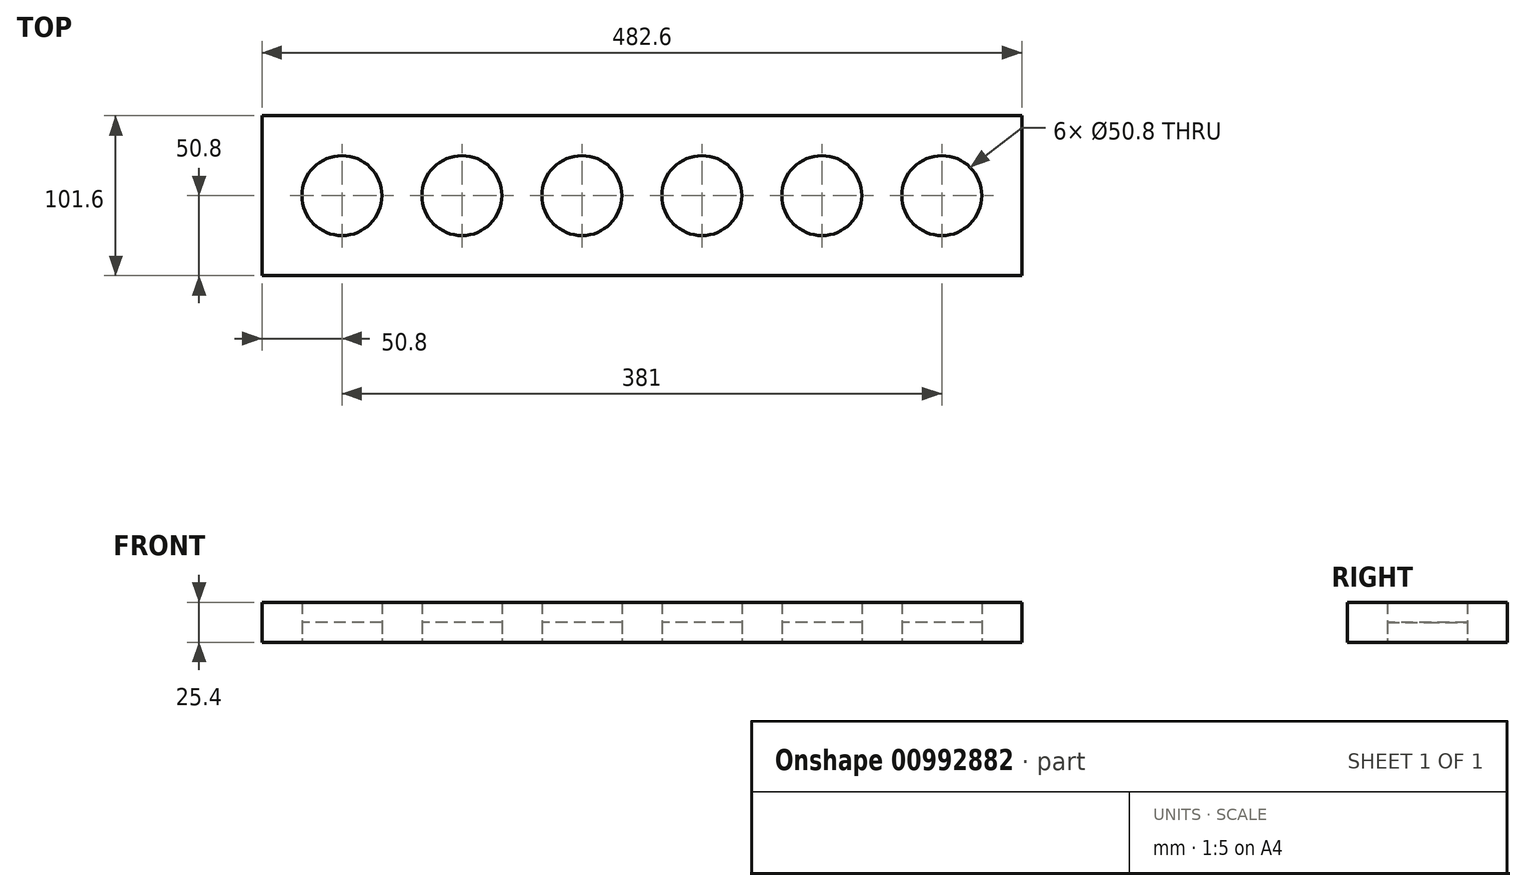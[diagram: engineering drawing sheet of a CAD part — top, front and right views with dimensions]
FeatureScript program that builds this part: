
annotation { "Feature Type Name" : "Feature", "Feature Type Description" : "" }
export const myFeature = defineFeature(function(context is Context, id is Id, definition is map)
    precondition{}
    {
        {
            var Q0;
            Q0=qCreatedBy(makeId("Top.planeOp"),FACE);
            var sketch = newSketch(context, id + "F0", { "sketchPlane" : qUnion([Q0])});
            skLineSegment(sketch, "E0.bottom", {"start": v(-241.3, -50.8) * mm, "end": v(241.3, -50.8) * mm});
            skLineSegment(sketch, "E0.top", {"start": v(-241.3, 50.8) * mm, "end": v(241.3, 50.8) * mm});
            skLineSegment(sketch, "E0.left", {"start": v(-241.3, -50.8) * mm, "end": v(-241.3, 50.8) * mm});
            skLineSegment(sketch, "E0.right", {"start": v(241.3, -50.8) * mm, "end": v(241.3, 50.8) * mm});
            skPoint(sketch, "E0.middle", {"position": v(0, 0) * mm});
            skCircle(sketch, "E1", {"center": v(-190.5, 0) * mm, "radius": 25.4 * mm});
            skCircle(sketch, "E2", {"center": v(-114.3, 0) * mm, "radius": 25.4 * mm});
            skCircle(sketch, "E3", {"center": v(-38.1, 0) * mm, "radius": 25.4 * mm});
            skCircle(sketch, "E4", {"center": v(38.1, 0) * mm, "radius": 25.4 * mm});
            skCircle(sketch, "E5", {"center": v(114.3, 0) * mm, "radius": 25.4 * mm});
            skCircle(sketch, "E6", {"center": v(190.5, 0) * mm, "radius": 25.4 * mm});
            skSolve(sketch);
        }
        {
            var Q0;
            Q0=makeQuery(id+"F0.imprint","IMPRINT",FACE,{"disambiguationData":[TD([[makeQuery(id+"F0.imprint","IMPRINT",EDGE,{"derivedFrom":sQuery(id+"F0.wireOp",EDGE,"E1")}),1.0]])]});
            var Q1;
            Q1=makeQuery(id+"F0.imprint","IMPRINT",FACE,{"disambiguationData":[TD([[makeQuery(id+"F0.imprint","IMPRINT",EDGE,{"derivedFrom":sQuery(id+"F0.wireOp",EDGE,"E2")}),1.0]])]});
            var Q2;
            Q2=makeQuery(id+"F0.imprint","IMPRINT",FACE,{"disambiguationData":[TD([[makeQuery(id+"F0.imprint","IMPRINT",EDGE,{"derivedFrom":sQuery(id+"F0.wireOp",EDGE,"E3")}),1.0]])]});
            var Q3;
            Q3=makeQuery(id+"F0.imprint","IMPRINT",FACE,{"disambiguationData":[TD([[makeQuery(id+"F0.imprint","IMPRINT",EDGE,{"derivedFrom":sQuery(id+"F0.wireOp",EDGE,"E4")}),1.0]])]});
            var Q4;
            Q4=makeQuery(id+"F0.imprint","IMPRINT",FACE,{"disambiguationData":[TD([[makeQuery(id+"F0.imprint","IMPRINT",EDGE,{"derivedFrom":sQuery(id+"F0.wireOp",EDGE,"E5")}),1.0]])]});
            var Q5;
            Q5=makeQuery(id+"F0.imprint","IMPRINT",FACE,{"disambiguationData":[TD([[makeQuery(id+"F0.imprint","IMPRINT",EDGE,{"derivedFrom":sQuery(id+"F0.wireOp",EDGE,"E6")}),1.0]])]});
            extrude(context, id + "F1", {"entities" : qUnion([Q0, Q1, Q2, Q3, Q4, Q5]), "depth" : 12.7 * mm, "offsetDistance" : 25.4 * mm});
        }
        {
            var Q0;
            Q0 = qSketchRegion(id + "F0", true);
            extrude(context, id + "F2", {"entities" : qUnion([Q0]), "depth" : 25.4 * mm, "offsetDistance" : 25.4 * mm});
        }
    });
